# Revit family: LAMP_MINI FLUT G2 ASYMMETRIC
name_source: partatom
category: Modelos genéricos
revit_build: Autodesk Revit 2015 (Build: 20140606_1530(x64)
units: mm (PartAtom-declared; Revit-internal decimal feet)

## types (8) — shared parameters
CRI = 70
Dimensions = 369 x 176 x 60
Elevación por defecto = 1219 mm
Fabricante = LAMP
Gear = Electronic
IEE = A+
Installation instructions = https://www.lamp.es
Insulation class = I
Lamp = HIGH POWER LED
Last update = 20/08/2019
Luminaire type = OUTDOOR - FLOODLIGHT
MacAdam = 4
Manufacturer URL = http://www.lamp.es
Manufacturer country = Spain
Manufacturer name = LAMP
Material Rótula = LAMP_Acero inoxidable AISI 304
Material cuerpo = LAMP_Aluminio Cuerpo Flut ANT
Model explanation = Availability of tilting between 0º and -30º (or 120º) when placed in a project.
Power Supply = 220-240V 50-60Hz
Product URL = https://www.lamp.es
Product datasheet = http://www.lamp.es
Protection rating = IP66 / IK06
Type = HIGH POWER PHILIPS
Weight = 4.10 kg

## per-type parameters (varying)
| type | Descripción | Efficacy | Finish | Initial color | Initial intensity | LED Lifetime | Modelo | Photometric web file | Plum | Power | Product code |
| 2733LM 3000 ANTHRACITE | MINI FLUT G2 3500 WW ASYM ANT. | 107 lm/W | Textured anthracite grey | 3000 K | 2733 lm | 50.000 L90 B10 | MF235AS730NA | Cuerpo MiniFlut G2 - Asym : 2733LM 3000 ANTHRACITE | 26 W | 23 W | MF235AS730NA |
| 2733LM 3000 GREY | MINI FLUT G2 3500 WW ASYM GR. | 107 lm/W | Texturised grey | 3000 K | 2733 lm | 50.000 L90 B10 | MF235AS730NG | Cuerpo MiniFlut G2 - Asym : 2733LM 3000 GREY | 26 W | 23 W | MF235AS730NG |
| 2877LM 4000 ANTHRACITE | MINI FLUT G2 3500 NW ASYM ANT. | 113 lm/W | Textured anthracite grey | 4000 K | 2877 lm | 50.000 L90 B10 | MF235AS740NA | Cuerpo MiniFlut G2 - Asym : 2877LM 4000 ANTHRACITE | 26 W | 23 W | MF235AS740NA |
| 2877LM 4000 GREY | MINI FLUT G2 3500 NW ASYM GR. | 113 lm/W | Texturised grey | 4000 K | 2877 lm | 50.000 L90 B10 | MF235AS740NG | Cuerpo MiniFlut G2 - Asym : 2877LM 4000 GREY | 26 W | 23 W | MF235AS740NG |
| 4990LM 3000 ANTHRACITE | MINI FLUT G2 6500 WW ASYM ANT. | 103 lm/W | Textured anthracite grey | 3000 K | 4990 lm | 60.000 L80 B10 | MF265AS730NA | Cuerpo MiniFlut G2 - Asym : 4990LM 3000 ANTHRACITE | 49 W | 44 W | MF265AS730NA |
| 4990LM 3000 GREY | MINI FLUT G2 6500 WW ASYM GR. | 103 lm/W | Texturised grey | 3000 K | 4990 lm | 60.000 L80 B10 | MF265AS730NG | Cuerpo MiniFlut G2 - Asym : 4990LM 3000 GREY | 49 W | 44 W | MF265AS730NG |
| 5253LM 4000 ANTHRACITE | MINI FLUT G2 6500 NW ASYM ANT. | 108 lm/W | Textured anthracite grey | 4000 K | 5253 lm | 60.000 L80 B10 | MF265AS740NA | Cuerpo MiniFlut G2 - Asym : 5253LM 4000 ANTHRACITE | 49 W | 44 W | MF265AS740NA |
| 5253LM 4000 GREY | MINI FLUT G2 6500 NW ASYM GR. | 108 lm/W | Texturised grey | 4000 K | 5253 lm | 60.000 L80 B10 | MF265AS740NG | Cuerpo MiniFlut G2 - Asym : 5253LM 4000 GREY | 49 W | 44 W | MF265AS740NG |
